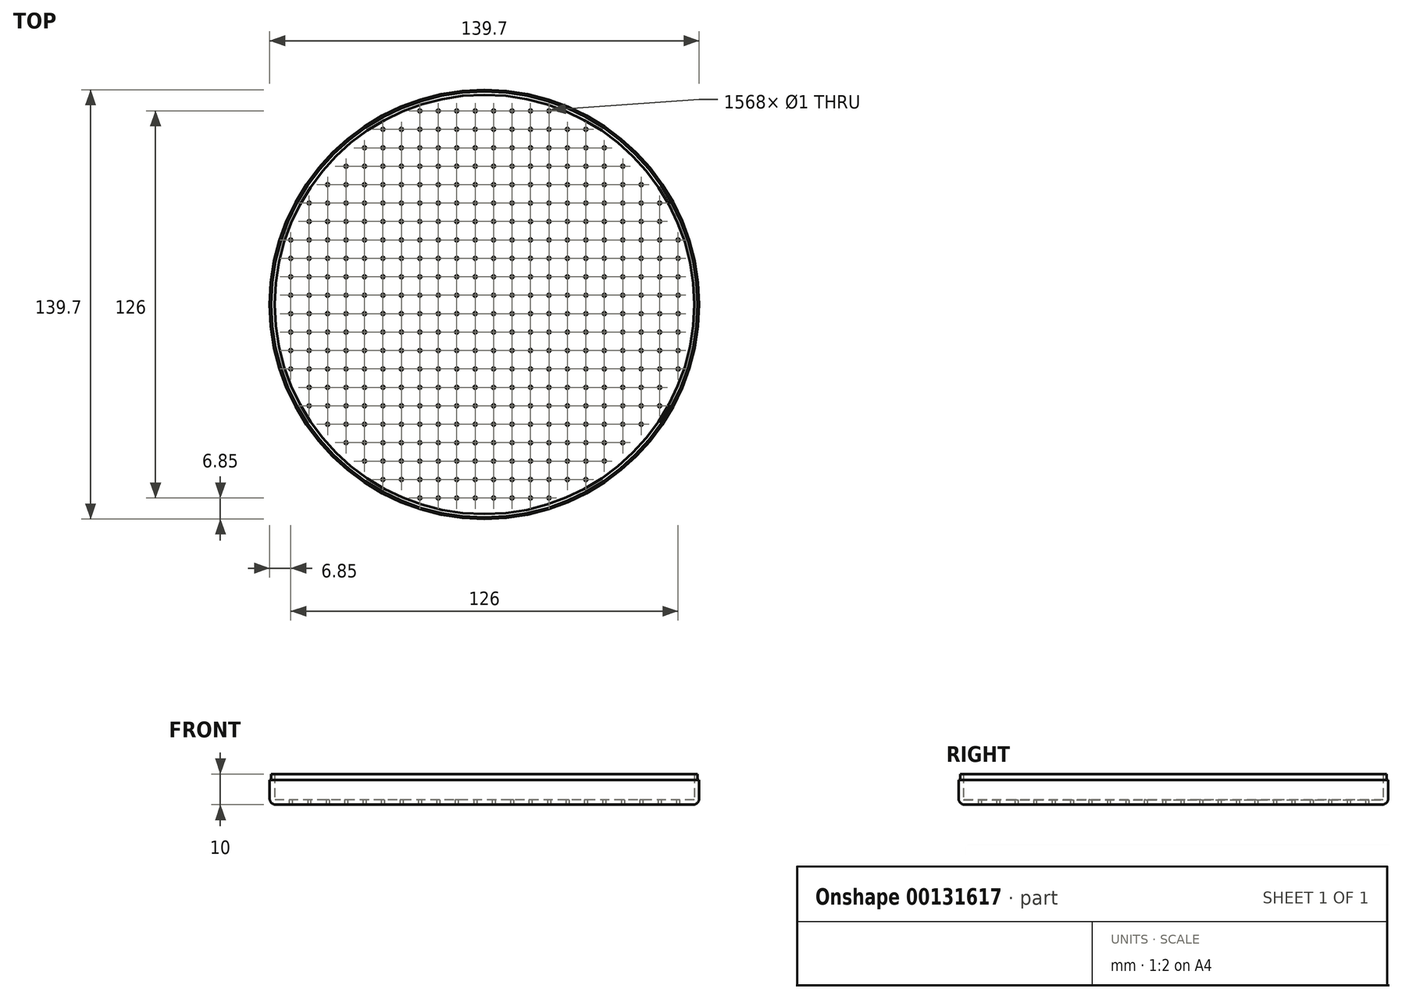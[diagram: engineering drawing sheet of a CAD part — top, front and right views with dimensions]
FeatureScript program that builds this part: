
annotation { "Feature Type Name" : "Feature", "Feature Type Description" : "" }
export const myFeature = defineFeature(function(context is Context, id is Id, definition is map)
    precondition{}
    {
        {
            var Q0;
            Q0=qCreatedBy(makeId("Top.planeOp"),FACE);
            var sketch = newSketch(context, id + "F0", { "sketchPlane" : qUnion([Q0])});
            skCircle(sketch, "E0", {"center": v(0, 0) * mm, "radius": 69.85 * mm});
            skSolve(sketch);
        }
        {
            var Q0;
            Q0 = qSketchRegion(id + "F0", true);
            extrude(context, id + "F1", {"entities" : qUnion([Q0]), "depth" : 10 * mm});
        }
        {
            var Q0;
            Q0=makeQuery(id+"F1.opExtrude","CAP_FACE",FACE,{"disambiguationData":[OSD([sQuery(id+"F0.wireOp",EDGE,"E0")])],"isStart":false});
            shell(context, id + "F2", {"entities" : qUnion([Q0]), "thickness" : 1.6 * mm});
        }
        {
            var Q0;
            Q0=makeQuery(id+"F1.opExtrude","CAP_FACE",FACE,{"disambiguationData":[OSD([sQuery(id+"F0.wireOp",EDGE,"E0")])],"isStart":true});
            var sketch = newSketch(context, id + "F3", { "sketchPlane" : qUnion([Q0])});
            skCircle(sketch, "E1", {"center": v(-3, 3) * mm, "radius": 0.5 * mm});
            skCircle(sketch, "E2.0.1.0", {"center": v(-3, 9) * mm, "radius": 0.5 * mm});
            skCircle(sketch, "E2.0.2.0", {"center": v(-3, 15) * mm, "radius": 0.5 * mm});
            skCircle(sketch, "E2.0.3.0", {"center": v(-3, 21) * mm, "radius": 0.5 * mm});
            skCircle(sketch, "E2.0.4.0", {"center": v(-3, 27) * mm, "radius": 0.5 * mm});
            skCircle(sketch, "E2.0.5.0", {"center": v(-3, 33) * mm, "radius": 0.5 * mm});
            skCircle(sketch, "E2.0.6.0", {"center": v(-3, 39) * mm, "radius": 0.5 * mm});
            skCircle(sketch, "E2.0.7.0", {"center": v(-3, 45) * mm, "radius": 0.5 * mm});
            skCircle(sketch, "E2.0.8.0", {"center": v(-3, 51) * mm, "radius": 0.5 * mm});
            skCircle(sketch, "E2.0.9.0", {"center": v(-3, 57) * mm, "radius": 0.5 * mm});
            skCircle(sketch, "E2.0.10.0", {"center": v(-3, 63) * mm, "radius": 0.5 * mm});
            skCircle(sketch, "E2.1.0.0", {"center": v(-9, 3) * mm, "radius": 0.5 * mm});
            skCircle(sketch, "E2.1.1.0", {"center": v(-9, 9) * mm, "radius": 0.5 * mm});
            skCircle(sketch, "E2.1.2.0", {"center": v(-9, 15) * mm, "radius": 0.5 * mm});
            skCircle(sketch, "E2.1.3.0", {"center": v(-9, 21) * mm, "radius": 0.5 * mm});
            skCircle(sketch, "E2.1.4.0", {"center": v(-9, 27) * mm, "radius": 0.5 * mm});
            skCircle(sketch, "E2.1.5.0", {"center": v(-9, 33) * mm, "radius": 0.5 * mm});
            skCircle(sketch, "E2.1.6.0", {"center": v(-9, 39) * mm, "radius": 0.5 * mm});
            skCircle(sketch, "E2.1.7.0", {"center": v(-9, 45) * mm, "radius": 0.5 * mm});
            skCircle(sketch, "E2.1.8.0", {"center": v(-9, 51) * mm, "radius": 0.5 * mm});
            skCircle(sketch, "E2.1.9.0", {"center": v(-9, 57) * mm, "radius": 0.5 * mm});
            skCircle(sketch, "E2.1.10.0", {"center": v(-9, 63) * mm, "radius": 0.5 * mm});
            skCircle(sketch, "E2.2.0.0", {"center": v(-15, 3) * mm, "radius": 0.5 * mm});
            skCircle(sketch, "E2.2.1.0", {"center": v(-15, 9) * mm, "radius": 0.5 * mm});
            skCircle(sketch, "E2.2.2.0", {"center": v(-15, 15) * mm, "radius": 0.5 * mm});
            skCircle(sketch, "E2.2.3.0", {"center": v(-15, 21) * mm, "radius": 0.5 * mm});
            skCircle(sketch, "E2.2.4.0", {"center": v(-15, 27) * mm, "radius": 0.5 * mm});
            skCircle(sketch, "E2.2.5.0", {"center": v(-15, 33) * mm, "radius": 0.5 * mm});
            skCircle(sketch, "E2.2.6.0", {"center": v(-15, 39) * mm, "radius": 0.5 * mm});
            skCircle(sketch, "E2.2.7.0", {"center": v(-15, 45) * mm, "radius": 0.5 * mm});
            skCircle(sketch, "E2.2.8.0", {"center": v(-15, 51) * mm, "radius": 0.5 * mm});
            skCircle(sketch, "E2.2.9.0", {"center": v(-15, 57) * mm, "radius": 0.5 * mm});
            skCircle(sketch, "E2.2.10.0", {"center": v(-15, 63) * mm, "radius": 0.5 * mm});
            skCircle(sketch, "E2.3.0.0", {"center": v(-21, 3) * mm, "radius": 0.5 * mm});
            skCircle(sketch, "E2.3.1.0", {"center": v(-21, 9) * mm, "radius": 0.5 * mm});
            skCircle(sketch, "E2.3.2.0", {"center": v(-21, 15) * mm, "radius": 0.5 * mm});
            skCircle(sketch, "E2.3.3.0", {"center": v(-21, 21) * mm, "radius": 0.5 * mm});
            skCircle(sketch, "E2.3.4.0", {"center": v(-21, 27) * mm, "radius": 0.5 * mm});
            skCircle(sketch, "E2.3.5.0", {"center": v(-21, 33) * mm, "radius": 0.5 * mm});
            skCircle(sketch, "E2.3.6.0", {"center": v(-21, 39) * mm, "radius": 0.5 * mm});
            skCircle(sketch, "E2.3.7.0", {"center": v(-21, 45) * mm, "radius": 0.5 * mm});
            skCircle(sketch, "E2.3.8.0", {"center": v(-21, 51) * mm, "radius": 0.5 * mm});
            skCircle(sketch, "E2.3.9.0", {"center": v(-21, 57) * mm, "radius": 0.5 * mm});
            skCircle(sketch, "E2.3.10.0", {"center": v(-21, 63) * mm, "radius": 0.5 * mm});
            skCircle(sketch, "E2.4.0.0", {"center": v(-27, 3) * mm, "radius": 0.5 * mm});
            skCircle(sketch, "E2.4.1.0", {"center": v(-27, 9) * mm, "radius": 0.5 * mm});
            skCircle(sketch, "E2.4.2.0", {"center": v(-27, 15) * mm, "radius": 0.5 * mm});
            skCircle(sketch, "E2.4.3.0", {"center": v(-27, 21) * mm, "radius": 0.5 * mm});
            skCircle(sketch, "E2.4.4.0", {"center": v(-27, 27) * mm, "radius": 0.5 * mm});
            skCircle(sketch, "E2.4.5.0", {"center": v(-27, 33) * mm, "radius": 0.5 * mm});
            skCircle(sketch, "E2.4.6.0", {"center": v(-27, 39) * mm, "radius": 0.5 * mm});
            skCircle(sketch, "E2.4.7.0", {"center": v(-27, 45) * mm, "radius": 0.5 * mm});
            skCircle(sketch, "E2.4.8.0", {"center": v(-27, 51) * mm, "radius": 0.5 * mm});
            skCircle(sketch, "E2.4.9.0", {"center": v(-27, 57) * mm, "radius": 0.5 * mm});
            skCircle(sketch, "E2.5.0.0", {"center": v(-33, 3) * mm, "radius": 0.5 * mm});
            skCircle(sketch, "E2.5.1.0", {"center": v(-33, 9) * mm, "radius": 0.5 * mm});
            skCircle(sketch, "E2.5.2.0", {"center": v(-33, 15) * mm, "radius": 0.5 * mm});
            skCircle(sketch, "E2.5.3.0", {"center": v(-33, 21) * mm, "radius": 0.5 * mm});
            skCircle(sketch, "E2.5.4.0", {"center": v(-33, 27) * mm, "radius": 0.5 * mm});
            skCircle(sketch, "E2.5.5.0", {"center": v(-33, 33) * mm, "radius": 0.5 * mm});
            skCircle(sketch, "E2.5.6.0", {"center": v(-33, 39) * mm, "radius": 0.5 * mm});
            skCircle(sketch, "E2.5.7.0", {"center": v(-33, 45) * mm, "radius": 0.5 * mm});
            skCircle(sketch, "E2.5.8.0", {"center": v(-33, 51) * mm, "radius": 0.5 * mm});
            skCircle(sketch, "E2.5.9.0", {"center": v(-33, 57) * mm, "radius": 0.5 * mm});
            skCircle(sketch, "E2.6.0.0", {"center": v(-39, 3) * mm, "radius": 0.5 * mm});
            skCircle(sketch, "E2.6.1.0", {"center": v(-39, 9) * mm, "radius": 0.5 * mm});
            skCircle(sketch, "E2.6.2.0", {"center": v(-39, 15) * mm, "radius": 0.5 * mm});
            skCircle(sketch, "E2.6.3.0", {"center": v(-39, 21) * mm, "radius": 0.5 * mm});
            skCircle(sketch, "E2.6.4.0", {"center": v(-39, 27) * mm, "radius": 0.5 * mm});
            skCircle(sketch, "E2.6.5.0", {"center": v(-39, 33) * mm, "radius": 0.5 * mm});
            skCircle(sketch, "E2.6.6.0", {"center": v(-39, 39) * mm, "radius": 0.5 * mm});
            skCircle(sketch, "E2.6.7.0", {"center": v(-39, 45) * mm, "radius": 0.5 * mm});
            skCircle(sketch, "E2.6.8.0", {"center": v(-39, 51) * mm, "radius": 0.5 * mm});
            skCircle(sketch, "E2.7.0.0", {"center": v(-45, 3) * mm, "radius": 0.5 * mm});
            skCircle(sketch, "E2.7.1.0", {"center": v(-45, 9) * mm, "radius": 0.5 * mm});
            skCircle(sketch, "E2.7.2.0", {"center": v(-45, 15) * mm, "radius": 0.5 * mm});
            skCircle(sketch, "E2.7.3.0", {"center": v(-45, 21) * mm, "radius": 0.5 * mm});
            skCircle(sketch, "E2.7.4.0", {"center": v(-45, 27) * mm, "radius": 0.5 * mm});
            skCircle(sketch, "E2.7.5.0", {"center": v(-45, 33) * mm, "radius": 0.5 * mm});
            skCircle(sketch, "E2.7.6.0", {"center": v(-45, 39) * mm, "radius": 0.5 * mm});
            skCircle(sketch, "E2.7.7.0", {"center": v(-45, 45) * mm, "radius": 0.5 * mm});
            skCircle(sketch, "E2.8.0.0", {"center": v(-51, 3) * mm, "radius": 0.5 * mm});
            skCircle(sketch, "E2.8.1.0", {"center": v(-51, 9) * mm, "radius": 0.5 * mm});
            skCircle(sketch, "E2.8.2.0", {"center": v(-51, 15) * mm, "radius": 0.5 * mm});
            skCircle(sketch, "E2.8.3.0", {"center": v(-51, 21) * mm, "radius": 0.5 * mm});
            skCircle(sketch, "E2.8.4.0", {"center": v(-51, 27) * mm, "radius": 0.5 * mm});
            skCircle(sketch, "E2.8.5.0", {"center": v(-51, 33) * mm, "radius": 0.5 * mm});
            skCircle(sketch, "E2.8.6.0", {"center": v(-51, 39) * mm, "radius": 0.5 * mm});
            skCircle(sketch, "E2.9.0.0", {"center": v(-57, 3) * mm, "radius": 0.5 * mm});
            skCircle(sketch, "E2.9.1.0", {"center": v(-57, 9) * mm, "radius": 0.5 * mm});
            skCircle(sketch, "E2.9.2.0", {"center": v(-57, 15) * mm, "radius": 0.5 * mm});
            skCircle(sketch, "E2.9.3.0", {"center": v(-57, 21) * mm, "radius": 0.5 * mm});
            skCircle(sketch, "E2.9.4.0", {"center": v(-57, 27) * mm, "radius": 0.5 * mm});
            skCircle(sketch, "E2.9.5.0", {"center": v(-57, 33) * mm, "radius": 0.5 * mm});
            skCircle(sketch, "E2.10.0.0", {"center": v(-63, 3) * mm, "radius": 0.5 * mm});
            skCircle(sketch, "E2.10.1.0", {"center": v(-63, 9) * mm, "radius": 0.5 * mm});
            skCircle(sketch, "E2.10.2.0", {"center": v(-63, 15) * mm, "radius": 0.5 * mm});
            skCircle(sketch, "E2.10.3.0", {"center": v(-63, 21) * mm, "radius": 0.5 * mm});
            skLineSegment(sketch, "E2.direction1", {"start": v(-3, 3) * mm, "end": v(-9, 3) * mm, "construction": true});
            skLineSegment(sketch, "E2.direction2", {"start": v(-3, 3) * mm, "end": v(-3, 9) * mm, "construction": true});
            skCircle(sketch, "E3.MirrorC", {"center": v(-3, -3) * mm, "radius": 0.5 * mm});
            skCircle(sketch, "E4.MirrorC", {"center": v(-9, -3) * mm, "radius": 0.5 * mm});
            skCircle(sketch, "E5.MirrorC", {"center": v(-3, -9) * mm, "radius": 0.5 * mm});
            skCircle(sketch, "E6.MirrorC", {"center": v(-51, -27) * mm, "radius": 0.5 * mm});
            skCircle(sketch, "E7.MirrorC", {"center": v(-57, -9) * mm, "radius": 0.5 * mm});
            skCircle(sketch, "E8.MirrorC", {"center": v(-21, -3) * mm, "radius": 0.5 * mm});
            skCircle(sketch, "E9.MirrorC", {"center": v(-15, -33) * mm, "radius": 0.5 * mm});
            skCircle(sketch, "E10.MirrorC", {"center": v(-27, -27) * mm, "radius": 0.5 * mm});
            skCircle(sketch, "E11.MirrorC", {"center": v(-21, -57) * mm, "radius": 0.5 * mm});
            skCircle(sketch, "E12.MirrorC", {"center": v(-33, -51) * mm, "radius": 0.5 * mm});
            skCircle(sketch, "E13.MirrorC", {"center": v(-33, -9) * mm, "radius": 0.5 * mm});
            skCircle(sketch, "E14.MirrorC", {"center": v(-45, -3) * mm, "radius": 0.5 * mm});
            skCircle(sketch, "E15.MirrorC", {"center": v(-39, -33) * mm, "radius": 0.5 * mm});
            skCircle(sketch, "E16.MirrorC", {"center": v(-9, -51) * mm, "radius": 0.5 * mm});
            skCircle(sketch, "E17.MirrorC", {"center": v(-39, -21) * mm, "radius": 0.5 * mm});
            skCircle(sketch, "E18.MirrorC", {"center": v(-45, -45) * mm, "radius": 0.5 * mm});
            skCircle(sketch, "E19.MirrorC", {"center": v(-63, -21) * mm, "radius": 0.5 * mm});
            skCircle(sketch, "E20.MirrorC", {"center": v(-15, -21) * mm, "radius": 0.5 * mm});
            skCircle(sketch, "E21.MirrorC", {"center": v(-21, -45) * mm, "radius": 0.5 * mm});
            skCircle(sketch, "E22.MirrorC", {"center": v(-51, -21) * mm, "radius": 0.5 * mm});
            skCircle(sketch, "E23.MirrorC", {"center": v(-27, -21) * mm, "radius": 0.5 * mm});
            skCircle(sketch, "E24.MirrorC", {"center": v(-33, -45) * mm, "radius": 0.5 * mm});
            skCircle(sketch, "E25.MirrorC", {"center": v(-9, -45) * mm, "radius": 0.5 * mm});
            skCircle(sketch, "E26.MirrorC", {"center": v(-39, -15) * mm, "radius": 0.5 * mm});
            skCircle(sketch, "E27.MirrorC", {"center": v(-45, -39) * mm, "radius": 0.5 * mm});
            skCircle(sketch, "E28.MirrorC", {"center": v(-63, -15) * mm, "radius": 0.5 * mm});
            skCircle(sketch, "E29.MirrorC", {"center": v(-15, -15) * mm, "radius": 0.5 * mm});
            skCircle(sketch, "E30.MirrorC", {"center": v(-21, -39) * mm, "radius": 0.5 * mm});
            skCircle(sketch, "E31.MirrorC", {"center": v(-3, -63) * mm, "radius": 0.5 * mm});
            skCircle(sketch, "E32.MirrorC", {"center": v(-3, -57) * mm, "radius": 0.5 * mm});
            skCircle(sketch, "E33.MirrorC", {"center": v(-3, -51) * mm, "radius": 0.5 * mm});
            skCircle(sketch, "E34.MirrorC", {"center": v(-3, -45) * mm, "radius": 0.5 * mm});
            skCircle(sketch, "E35.MirrorC", {"center": v(-3, -39) * mm, "radius": 0.5 * mm});
            skCircle(sketch, "E36.MirrorC", {"center": v(-3, -33) * mm, "radius": 0.5 * mm});
            skCircle(sketch, "E37.MirrorC", {"center": v(-3, -27) * mm, "radius": 0.5 * mm});
            skCircle(sketch, "E38.MirrorC", {"center": v(-3, -21) * mm, "radius": 0.5 * mm});
            skCircle(sketch, "E39.MirrorC", {"center": v(-3, -15) * mm, "radius": 0.5 * mm});
            skCircle(sketch, "E40.MirrorC", {"center": v(-51, -15) * mm, "radius": 0.5 * mm});
            skCircle(sketch, "E41.MirrorC", {"center": v(-15, -63) * mm, "radius": 0.5 * mm});
            skCircle(sketch, "E42.MirrorC", {"center": v(-27, -15) * mm, "radius": 0.5 * mm});
            skCircle(sketch, "E43.MirrorC", {"center": v(-33, -39) * mm, "radius": 0.5 * mm});
            skCircle(sketch, "E44.MirrorC", {"center": v(-9, -21) * mm, "radius": 0.5 * mm});
            skCircle(sketch, "E45.MirrorC", {"center": v(-9, -15) * mm, "radius": 0.5 * mm});
            skCircle(sketch, "E46.MirrorC", {"center": v(-9, -39) * mm, "radius": 0.5 * mm});
            skCircle(sketch, "E47.MirrorC", {"center": v(-9, -9) * mm, "radius": 0.5 * mm});
            skCircle(sketch, "E48.MirrorC", {"center": v(-39, -9) * mm, "radius": 0.5 * mm});
            skCircle(sketch, "E49.MirrorC", {"center": v(-45, -33) * mm, "radius": 0.5 * mm});
            skCircle(sketch, "E50.MirrorC", {"center": v(-63, -9) * mm, "radius": 0.5 * mm});
            skCircle(sketch, "E51.MirrorC", {"center": v(-15, -9) * mm, "radius": 0.5 * mm});
            skCircle(sketch, "E52.MirrorC", {"center": v(-21, -33) * mm, "radius": 0.5 * mm});
            skCircle(sketch, "E53.MirrorC", {"center": v(-27, -57) * mm, "radius": 0.5 * mm});
            skCircle(sketch, "E54.MirrorC", {"center": v(-15, -57) * mm, "radius": 0.5 * mm});
            skCircle(sketch, "E55.MirrorC", {"center": v(-27, -9) * mm, "radius": 0.5 * mm});
            skCircle(sketch, "E56.MirrorC", {"center": v(-33, -33) * mm, "radius": 0.5 * mm});
            skCircle(sketch, "E57.MirrorC", {"center": v(-9, -33) * mm, "radius": 0.5 * mm});
            skCircle(sketch, "E58.MirrorC", {"center": v(-39, -3) * mm, "radius": 0.5 * mm});
            skCircle(sketch, "E59.MirrorC", {"center": v(-45, -27) * mm, "radius": 0.5 * mm});
            skCircle(sketch, "E60.MirrorC", {"center": v(-63, -3) * mm, "radius": 0.5 * mm});
            skCircle(sketch, "E61.MirrorC", {"center": v(-15, -3) * mm, "radius": 0.5 * mm});
            skCircle(sketch, "E62.MirrorC", {"center": v(-21, -27) * mm, "radius": 0.5 * mm});
            skCircle(sketch, "E63.MirrorC", {"center": v(-27, -51) * mm, "radius": 0.5 * mm});
            skCircle(sketch, "E64.MirrorC", {"center": v(-51, -9) * mm, "radius": 0.5 * mm});
            skCircle(sketch, "E65.MirrorC", {"center": v(-57, -33) * mm, "radius": 0.5 * mm});
            skCircle(sketch, "E66.MirrorC", {"center": v(-45, -21) * mm, "radius": 0.5 * mm});
            skCircle(sketch, "E67.MirrorC", {"center": v(-9, -27) * mm, "radius": 0.5 * mm});
            skCircle(sketch, "E68.MirrorC", {"center": v(-21, -21) * mm, "radius": 0.5 * mm});
            skCircle(sketch, "E69.MirrorC", {"center": v(-27, -45) * mm, "radius": 0.5 * mm});
            skCircle(sketch, "E70.MirrorC", {"center": v(-51, -3) * mm, "radius": 0.5 * mm});
            skCircle(sketch, "E71.MirrorC", {"center": v(-57, -27) * mm, "radius": 0.5 * mm});
            skLineSegment(sketch, "E72.MirrorCS", {"start": v(-3, -3) * mm, "end": v(-3, -9) * mm, "construction": true});
            skLineSegment(sketch, "E73.MirrorCS", {"start": v(-3, -3) * mm, "end": v(-9, -3) * mm, "construction": true});
            skCircle(sketch, "E74.MirrorC", {"center": v(-15, -51) * mm, "radius": 0.5 * mm});
            skCircle(sketch, "E75.MirrorC", {"center": v(-27, -3) * mm, "radius": 0.5 * mm});
            skCircle(sketch, "E76.MirrorC", {"center": v(-33, -27) * mm, "radius": 0.5 * mm});
            skCircle(sketch, "E77.MirrorC", {"center": v(-39, -51) * mm, "radius": 0.5 * mm});
            skCircle(sketch, "E78.MirrorC", {"center": v(-51, -39) * mm, "radius": 0.5 * mm});
            skCircle(sketch, "E79.MirrorC", {"center": v(-57, -21) * mm, "radius": 0.5 * mm});
            skCircle(sketch, "E80.MirrorC", {"center": v(-21, -15) * mm, "radius": 0.5 * mm});
            skCircle(sketch, "E81.MirrorC", {"center": v(-15, -45) * mm, "radius": 0.5 * mm});
            skCircle(sketch, "E82.MirrorC", {"center": v(-27, -39) * mm, "radius": 0.5 * mm});
            skCircle(sketch, "E83.MirrorC", {"center": v(-33, -21) * mm, "radius": 0.5 * mm});
            skCircle(sketch, "E84.MirrorC", {"center": v(-45, -15) * mm, "radius": 0.5 * mm});
            skCircle(sketch, "E85.MirrorC", {"center": v(-39, -45) * mm, "radius": 0.5 * mm});
            skCircle(sketch, "E86.MirrorC", {"center": v(-9, -63) * mm, "radius": 0.5 * mm});
            skCircle(sketch, "E87.MirrorC", {"center": v(-51, -33) * mm, "radius": 0.5 * mm});
            skCircle(sketch, "E88.MirrorC", {"center": v(-57, -15) * mm, "radius": 0.5 * mm});
            skCircle(sketch, "E89.MirrorC", {"center": v(-21, -9) * mm, "radius": 0.5 * mm});
            skCircle(sketch, "E90.MirrorC", {"center": v(-15, -39) * mm, "radius": 0.5 * mm});
            skCircle(sketch, "E91.MirrorC", {"center": v(-27, -33) * mm, "radius": 0.5 * mm});
            skCircle(sketch, "E92.MirrorC", {"center": v(-21, -63) * mm, "radius": 0.5 * mm});
            skCircle(sketch, "E93.MirrorC", {"center": v(-33, -57) * mm, "radius": 0.5 * mm});
            skCircle(sketch, "E94.MirrorC", {"center": v(-33, -15) * mm, "radius": 0.5 * mm});
            skCircle(sketch, "E95.MirrorC", {"center": v(-45, -9) * mm, "radius": 0.5 * mm});
            skCircle(sketch, "E96.MirrorC", {"center": v(-39, -39) * mm, "radius": 0.5 * mm});
            skCircle(sketch, "E97.MirrorC", {"center": v(-9, -57) * mm, "radius": 0.5 * mm});
            skCircle(sketch, "E98.MirrorC", {"center": v(-39, -27) * mm, "radius": 0.5 * mm});
            skCircle(sketch, "E99.MirrorC", {"center": v(-57, -3) * mm, "radius": 0.5 * mm});
            skCircle(sketch, "E100.MirrorC", {"center": v(-15, -27) * mm, "radius": 0.5 * mm});
            skCircle(sketch, "E101.MirrorC", {"center": v(-21, -51) * mm, "radius": 0.5 * mm});
            skCircle(sketch, "E102.MirrorC", {"center": v(-33, -3) * mm, "radius": 0.5 * mm});
            skCircle(sketch, "E103.MirrorC", {"center": v(3, 3) * mm, "radius": 0.5 * mm});
            skCircle(sketch, "E104.MirrorC", {"center": v(3, -3) * mm, "radius": 0.5 * mm});
            skCircle(sketch, "E105.MirrorC", {"center": v(9, 3) * mm, "radius": 0.5 * mm});
            skCircle(sketch, "E106.MirrorC", {"center": v(3, 9) * mm, "radius": 0.5 * mm});
            skLineSegment(sketch, "E107.MirrorCS", {"start": v(3, -3) * mm, "end": v(9, -3) * mm, "construction": true});
            skLineSegment(sketch, "E108.MirrorCS", {"start": v(3, -3) * mm, "end": v(3, -9) * mm, "construction": true});
            skLineSegment(sketch, "E109.MirrorCS", {"start": v(3, 3) * mm, "end": v(3, 9) * mm, "construction": true});
            skLineSegment(sketch, "E110.MirrorCS", {"start": v(3, 3) * mm, "end": v(9, 3) * mm, "construction": true});
            skCircle(sketch, "E111.MirrorC", {"center": v(3, -9) * mm, "radius": 0.5 * mm});
            skCircle(sketch, "E112.MirrorC", {"center": v(9, -3) * mm, "radius": 0.5 * mm});
            skCircle(sketch, "E113.MirrorC", {"center": v(3, 63) * mm, "radius": 0.5 * mm});
            skCircle(sketch, "E114.MirrorC", {"center": v(3, 57) * mm, "radius": 0.5 * mm});
            skCircle(sketch, "E115.MirrorC", {"center": v(3, 51) * mm, "radius": 0.5 * mm});
            skCircle(sketch, "E116.MirrorC", {"center": v(3, 45) * mm, "radius": 0.5 * mm});
            skCircle(sketch, "E117.MirrorC", {"center": v(3, 39) * mm, "radius": 0.5 * mm});
            skCircle(sketch, "E118.MirrorC", {"center": v(3, 33) * mm, "radius": 0.5 * mm});
            skCircle(sketch, "E119.MirrorC", {"center": v(3, 27) * mm, "radius": 0.5 * mm});
            skCircle(sketch, "E120.MirrorC", {"center": v(3, 21) * mm, "radius": 0.5 * mm});
            skCircle(sketch, "E121.MirrorC", {"center": v(3, 15) * mm, "radius": 0.5 * mm});
            skCircle(sketch, "E122.MirrorC", {"center": v(9, 21) * mm, "radius": 0.5 * mm});
            skCircle(sketch, "E123.MirrorC", {"center": v(9, 15) * mm, "radius": 0.5 * mm});
            skCircle(sketch, "E124.MirrorC", {"center": v(9, 9) * mm, "radius": 0.5 * mm});
            skCircle(sketch, "E125.MirrorC", {"center": v(51, -33) * mm, "radius": 0.5 * mm});
            skCircle(sketch, "E126.MirrorC", {"center": v(33, -39) * mm, "radius": 0.5 * mm});
            skCircle(sketch, "E127.MirrorC", {"center": v(27, -9) * mm, "radius": 0.5 * mm});
            skCircle(sketch, "E128.MirrorC", {"center": v(45, -21) * mm, "radius": 0.5 * mm});
            skCircle(sketch, "E129.MirrorC", {"center": v(51, -39) * mm, "radius": 0.5 * mm});
            skCircle(sketch, "E130.MirrorC", {"center": v(21, -3) * mm, "radius": 0.5 * mm});
            skCircle(sketch, "E131.MirrorC", {"center": v(39, 27) * mm, "radius": 0.5 * mm});
            skCircle(sketch, "E132.MirrorC", {"center": v(57, 3) * mm, "radius": 0.5 * mm});
            skCircle(sketch, "E133.MirrorC", {"center": v(15, 27) * mm, "radius": 0.5 * mm});
            skCircle(sketch, "E134.MirrorC", {"center": v(21, 51) * mm, "radius": 0.5 * mm});
            skCircle(sketch, "E135.MirrorC", {"center": v(33, 3) * mm, "radius": 0.5 * mm});
            skCircle(sketch, "E136.MirrorC", {"center": v(9, -63) * mm, "radius": 0.5 * mm});
            skCircle(sketch, "E137.MirrorC", {"center": v(9, -57) * mm, "radius": 0.5 * mm});
            skCircle(sketch, "E138.MirrorC", {"center": v(27, -15) * mm, "radius": 0.5 * mm});
            skCircle(sketch, "E139.MirrorC", {"center": v(15, -57) * mm, "radius": 0.5 * mm});
            skCircle(sketch, "E140.MirrorC", {"center": v(39, -51) * mm, "radius": 0.5 * mm});
            skCircle(sketch, "E141.MirrorC", {"center": v(21, -45) * mm, "radius": 0.5 * mm});
            skCircle(sketch, "E142.MirrorC", {"center": v(21, -39) * mm, "radius": 0.5 * mm});
            skCircle(sketch, "E143.MirrorC", {"center": v(39, 21) * mm, "radius": 0.5 * mm});
            skCircle(sketch, "E144.MirrorC", {"center": v(45, 45) * mm, "radius": 0.5 * mm});
            skCircle(sketch, "E145.MirrorC", {"center": v(63, 21) * mm, "radius": 0.5 * mm});
            skCircle(sketch, "E146.MirrorC", {"center": v(15, 21) * mm, "radius": 0.5 * mm});
            skCircle(sketch, "E147.MirrorC", {"center": v(21, 45) * mm, "radius": 0.5 * mm});
            skCircle(sketch, "E148.MirrorC", {"center": v(39, -45) * mm, "radius": 0.5 * mm});
            skCircle(sketch, "E149.MirrorC", {"center": v(39, -39) * mm, "radius": 0.5 * mm});
            skCircle(sketch, "E150.MirrorC", {"center": v(15, -63) * mm, "radius": 0.5 * mm});
            skCircle(sketch, "E151.MirrorC", {"center": v(33, -27) * mm, "radius": 0.5 * mm});
            skCircle(sketch, "E152.MirrorC", {"center": v(15, -21) * mm, "radius": 0.5 * mm});
            skCircle(sketch, "E153.MirrorC", {"center": v(15, -15) * mm, "radius": 0.5 * mm});
            skCircle(sketch, "E154.MirrorC", {"center": v(39, 15) * mm, "radius": 0.5 * mm});
            skCircle(sketch, "E155.MirrorC", {"center": v(45, 39) * mm, "radius": 0.5 * mm});
            skCircle(sketch, "E156.MirrorC", {"center": v(63, 15) * mm, "radius": 0.5 * mm});
            skCircle(sketch, "E157.MirrorC", {"center": v(15, 15) * mm, "radius": 0.5 * mm});
            skCircle(sketch, "E158.MirrorC", {"center": v(21, 39) * mm, "radius": 0.5 * mm});
            skCircle(sketch, "E159.MirrorC", {"center": v(45, -15) * mm, "radius": 0.5 * mm});
            skCircle(sketch, "E160.MirrorC", {"center": v(45, -9) * mm, "radius": 0.5 * mm});
            skCircle(sketch, "E161.MirrorC", {"center": v(27, -57) * mm, "radius": 0.5 * mm});
            skCircle(sketch, "E162.MirrorC", {"center": v(27, -3) * mm, "radius": 0.5 * mm});
            skCircle(sketch, "E163.MirrorC", {"center": v(63, -21) * mm, "radius": 0.5 * mm});
            skCircle(sketch, "E164.MirrorC", {"center": v(63, -15) * mm, "radius": 0.5 * mm});
            skCircle(sketch, "E165.MirrorC", {"center": v(39, 9) * mm, "radius": 0.5 * mm});
            skCircle(sketch, "E166.MirrorC", {"center": v(45, 33) * mm, "radius": 0.5 * mm});
            skCircle(sketch, "E167.MirrorC", {"center": v(63, 9) * mm, "radius": 0.5 * mm});
            skCircle(sketch, "E168.MirrorC", {"center": v(15, 9) * mm, "radius": 0.5 * mm});
            skCircle(sketch, "E169.MirrorC", {"center": v(21, 33) * mm, "radius": 0.5 * mm});
            skCircle(sketch, "E170.MirrorC", {"center": v(27, 57) * mm, "radius": 0.5 * mm});
            skCircle(sketch, "E171.MirrorC", {"center": v(33, -21) * mm, "radius": 0.5 * mm});
            skCircle(sketch, "E172.MirrorC", {"center": v(33, -15) * mm, "radius": 0.5 * mm});
            skCircle(sketch, "E173.MirrorC", {"center": v(21, -33) * mm, "radius": 0.5 * mm});
            skCircle(sketch, "E174.MirrorC", {"center": v(57, -33) * mm, "radius": 0.5 * mm});
            skCircle(sketch, "E175.MirrorC", {"center": v(15, -51) * mm, "radius": 0.5 * mm});
            skCircle(sketch, "E176.MirrorC", {"center": v(57, -9) * mm, "radius": 0.5 * mm});
            skCircle(sketch, "E177.MirrorC", {"center": v(39, 3) * mm, "radius": 0.5 * mm});
            skCircle(sketch, "E178.MirrorC", {"center": v(45, 27) * mm, "radius": 0.5 * mm});
            skCircle(sketch, "E179.MirrorC", {"center": v(63, 3) * mm, "radius": 0.5 * mm});
            skCircle(sketch, "E180.MirrorC", {"center": v(15, 3) * mm, "radius": 0.5 * mm});
            skCircle(sketch, "E181.MirrorC", {"center": v(21, 27) * mm, "radius": 0.5 * mm});
            skCircle(sketch, "E182.MirrorC", {"center": v(27, 51) * mm, "radius": 0.5 * mm});
            skCircle(sketch, "E183.MirrorC", {"center": v(33, -57) * mm, "radius": 0.5 * mm});
            skCircle(sketch, "E184.MirrorC", {"center": v(51, -15) * mm, "radius": 0.5 * mm});
            skCircle(sketch, "E185.MirrorC", {"center": v(15, -9) * mm, "radius": 0.5 * mm});
            skCircle(sketch, "E186.MirrorC", {"center": v(51, -9) * mm, "radius": 0.5 * mm});
            skCircle(sketch, "E187.MirrorC", {"center": v(45, -45) * mm, "radius": 0.5 * mm});
            skCircle(sketch, "E188.MirrorC", {"center": v(45, -39) * mm, "radius": 0.5 * mm});
            skCircle(sketch, "E189.MirrorC", {"center": v(45, 21) * mm, "radius": 0.5 * mm});
            skCircle(sketch, "E190.MirrorC", {"center": v(39, 51) * mm, "radius": 0.5 * mm});
            skCircle(sketch, "E191.MirrorC", {"center": v(33, 27) * mm, "radius": 0.5 * mm});
            skCircle(sketch, "E192.MirrorC", {"center": v(27, -51) * mm, "radius": 0.5 * mm});
            skCircle(sketch, "E193.MirrorC", {"center": v(27, 3) * mm, "radius": 0.5 * mm});
            skCircle(sketch, "E194.MirrorC", {"center": v(15, 51) * mm, "radius": 0.5 * mm});
            skCircle(sketch, "E195.MirrorC", {"center": v(57, 27) * mm, "radius": 0.5 * mm});
            skCircle(sketch, "E196.MirrorC", {"center": v(51, 3) * mm, "radius": 0.5 * mm});
            skCircle(sketch, "E197.MirrorC", {"center": v(9, -39) * mm, "radius": 0.5 * mm});
            skCircle(sketch, "E198.MirrorC", {"center": v(3, -51) * mm, "radius": 0.5 * mm});
            skCircle(sketch, "E199.MirrorC", {"center": v(33, -51) * mm, "radius": 0.5 * mm});
            skCircle(sketch, "E200.MirrorC", {"center": v(39, -3) * mm, "radius": 0.5 * mm});
            skCircle(sketch, "E201.MirrorC", {"center": v(9, 27) * mm, "radius": 0.5 * mm});
            skCircle(sketch, "E202.MirrorC", {"center": v(39, -27) * mm, "radius": 0.5 * mm});
            skCircle(sketch, "E203.MirrorC", {"center": v(39, 33) * mm, "radius": 0.5 * mm});
            skCircle(sketch, "E204.MirrorC", {"center": v(33, 9) * mm, "radius": 0.5 * mm});
            skCircle(sketch, "E205.MirrorC", {"center": v(21, 57) * mm, "radius": 0.5 * mm});
            skCircle(sketch, "E206.MirrorC", {"center": v(15, 33) * mm, "radius": 0.5 * mm});
            skCircle(sketch, "E207.MirrorC", {"center": v(9, 51) * mm, "radius": 0.5 * mm});
            skCircle(sketch, "E208.MirrorC", {"center": v(57, 9) * mm, "radius": 0.5 * mm});
            skCircle(sketch, "E209.MirrorC", {"center": v(45, 3) * mm, "radius": 0.5 * mm});
            skCircle(sketch, "E210.MirrorC", {"center": v(33, 51) * mm, "radius": 0.5 * mm});
            skCircle(sketch, "E211.MirrorC", {"center": v(57, 33) * mm, "radius": 0.5 * mm});
            skCircle(sketch, "E212.MirrorC", {"center": v(27, 27) * mm, "radius": 0.5 * mm});
            skCircle(sketch, "E213.MirrorC", {"center": v(21, 3) * mm, "radius": 0.5 * mm});
            skCircle(sketch, "E214.MirrorC", {"center": v(9, -21) * mm, "radius": 0.5 * mm});
            skCircle(sketch, "E215.MirrorC", {"center": v(51, 9) * mm, "radius": 0.5 * mm});
            skCircle(sketch, "E216.MirrorC", {"center": v(9, -9) * mm, "radius": 0.5 * mm});
            skCircle(sketch, "E217.MirrorC", {"center": v(3, -45) * mm, "radius": 0.5 * mm});
            skCircle(sketch, "E218.MirrorC", {"center": v(51, -21) * mm, "radius": 0.5 * mm});
            skCircle(sketch, "E219.MirrorC", {"center": v(27, -21) * mm, "radius": 0.5 * mm});
            skCircle(sketch, "E220.MirrorC", {"center": v(51, 27) * mm, "radius": 0.5 * mm});
            skCircle(sketch, "E221.MirrorC", {"center": v(15, -33) * mm, "radius": 0.5 * mm});
            skCircle(sketch, "E222.MirrorC", {"center": v(33, -9) * mm, "radius": 0.5 * mm});
            skCircle(sketch, "E223.MirrorC", {"center": v(33, -33) * mm, "radius": 0.5 * mm});
            skCircle(sketch, "E224.MirrorC", {"center": v(45, -33) * mm, "radius": 0.5 * mm});
            skCircle(sketch, "E225.MirrorC", {"center": v(3, -27) * mm, "radius": 0.5 * mm});
            skCircle(sketch, "E226.MirrorC", {"center": v(9, -51) * mm, "radius": 0.5 * mm});
            skCircle(sketch, "E227.MirrorC", {"center": v(9, -45) * mm, "radius": 0.5 * mm});
            skCircle(sketch, "E228.MirrorC", {"center": v(15, -39) * mm, "radius": 0.5 * mm});
            skCircle(sketch, "E229.MirrorC", {"center": v(15, -45) * mm, "radius": 0.5 * mm});
            skCircle(sketch, "E230.MirrorC", {"center": v(21, -21) * mm, "radius": 0.5 * mm});
            skCircle(sketch, "E231.MirrorC", {"center": v(15, -3) * mm, "radius": 0.5 * mm});
            skCircle(sketch, "E232.MirrorC", {"center": v(57, -27) * mm, "radius": 0.5 * mm});
            skCircle(sketch, "E233.MirrorC", {"center": v(45, -27) * mm, "radius": 0.5 * mm});
            skCircle(sketch, "E234.MirrorC", {"center": v(15, -27) * mm, "radius": 0.5 * mm});
            skCircle(sketch, "E235.MirrorC", {"center": v(39, 39) * mm, "radius": 0.5 * mm});
            skCircle(sketch, "E236.MirrorC", {"center": v(33, 15) * mm, "radius": 0.5 * mm});
            skCircle(sketch, "E237.MirrorC", {"center": v(21, 63) * mm, "radius": 0.5 * mm});
            skCircle(sketch, "E238.MirrorC", {"center": v(9, 33) * mm, "radius": 0.5 * mm});
            skCircle(sketch, "E239.MirrorC", {"center": v(33, 33) * mm, "radius": 0.5 * mm});
            skCircle(sketch, "E240.MirrorC", {"center": v(27, 9) * mm, "radius": 0.5 * mm});
            skCircle(sketch, "E241.MirrorC", {"center": v(15, 57) * mm, "radius": 0.5 * mm});
            skCircle(sketch, "E242.MirrorC", {"center": v(15, 39) * mm, "radius": 0.5 * mm});
            skCircle(sketch, "E243.MirrorC", {"center": v(57, 15) * mm, "radius": 0.5 * mm});
            skCircle(sketch, "E244.MirrorC", {"center": v(3, -63) * mm, "radius": 0.5 * mm});
            skCircle(sketch, "E245.MirrorC", {"center": v(3, -39) * mm, "radius": 0.5 * mm});
            skCircle(sketch, "E246.MirrorC", {"center": v(33, -45) * mm, "radius": 0.5 * mm});
            skCircle(sketch, "E247.MirrorC", {"center": v(45, -3) * mm, "radius": 0.5 * mm});
            skCircle(sketch, "E248.MirrorC", {"center": v(27, -45) * mm, "radius": 0.5 * mm});
            skCircle(sketch, "E249.MirrorC", {"center": v(21, -51) * mm, "radius": 0.5 * mm});
            skCircle(sketch, "E250.MirrorC", {"center": v(27, -27) * mm, "radius": 0.5 * mm});
            skCircle(sketch, "E251.MirrorC", {"center": v(9, 57) * mm, "radius": 0.5 * mm});
            skCircle(sketch, "E252.MirrorC", {"center": v(45, 9) * mm, "radius": 0.5 * mm});
            skCircle(sketch, "E253.MirrorC", {"center": v(33, 57) * mm, "radius": 0.5 * mm});
            skCircle(sketch, "E254.MirrorC", {"center": v(27, 33) * mm, "radius": 0.5 * mm});
            skCircle(sketch, "E255.MirrorC", {"center": v(21, 9) * mm, "radius": 0.5 * mm});
            skCircle(sketch, "E256.MirrorC", {"center": v(9, 39) * mm, "radius": 0.5 * mm});
            skCircle(sketch, "E257.MirrorC", {"center": v(51, -27) * mm, "radius": 0.5 * mm});
            skCircle(sketch, "E258.MirrorC", {"center": v(51, 33) * mm, "radius": 0.5 * mm});
            skCircle(sketch, "E259.MirrorC", {"center": v(33, 39) * mm, "radius": 0.5 * mm});
            skCircle(sketch, "E260.MirrorC", {"center": v(27, 15) * mm, "radius": 0.5 * mm});
            skCircle(sketch, "E261.MirrorC", {"center": v(15, 63) * mm, "radius": 0.5 * mm});
            skCircle(sketch, "E262.MirrorC", {"center": v(3, -21) * mm, "radius": 0.5 * mm});
            skCircle(sketch, "E263.MirrorC", {"center": v(27, -33) * mm, "radius": 0.5 * mm});
            skCircle(sketch, "E264.MirrorC", {"center": v(27, -39) * mm, "radius": 0.5 * mm});
            skCircle(sketch, "E265.MirrorC", {"center": v(21, -27) * mm, "radius": 0.5 * mm});
            skCircle(sketch, "E266.MirrorC", {"center": v(51, 15) * mm, "radius": 0.5 * mm});
            skCircle(sketch, "E267.MirrorC", {"center": v(21, -9) * mm, "radius": 0.5 * mm});
            skCircle(sketch, "E268.MirrorC", {"center": v(21, -15) * mm, "radius": 0.5 * mm});
            skCircle(sketch, "E269.MirrorC", {"center": v(51, -3) * mm, "radius": 0.5 * mm});
            skCircle(sketch, "E270.MirrorC", {"center": v(63, -3) * mm, "radius": 0.5 * mm});
            skCircle(sketch, "E271.MirrorC", {"center": v(33, -3) * mm, "radius": 0.5 * mm});
            skCircle(sketch, "E272.MirrorC", {"center": v(9, 63) * mm, "radius": 0.5 * mm});
            skCircle(sketch, "E273.MirrorC", {"center": v(45, 15) * mm, "radius": 0.5 * mm});
            skCircle(sketch, "E274.MirrorC", {"center": v(27, 39) * mm, "radius": 0.5 * mm});
            skCircle(sketch, "E275.MirrorC", {"center": v(21, 15) * mm, "radius": 0.5 * mm});
            skCircle(sketch, "E276.MirrorC", {"center": v(27, 45) * mm, "radius": 0.5 * mm});
            skCircle(sketch, "E277.MirrorC", {"center": v(21, 21) * mm, "radius": 0.5 * mm});
            skCircle(sketch, "E278.MirrorC", {"center": v(39, 45) * mm, "radius": 0.5 * mm});
            skCircle(sketch, "E279.MirrorC", {"center": v(33, 21) * mm, "radius": 0.5 * mm});
            skCircle(sketch, "E280.MirrorC", {"center": v(15, 45) * mm, "radius": 0.5 * mm});
            skCircle(sketch, "E281.MirrorC", {"center": v(57, 21) * mm, "radius": 0.5 * mm});
            skCircle(sketch, "E282.MirrorC", {"center": v(9, -15) * mm, "radius": 0.5 * mm});
            skCircle(sketch, "E283.MirrorC", {"center": v(3, -57) * mm, "radius": 0.5 * mm});
            skCircle(sketch, "E284.MirrorC", {"center": v(9, 45) * mm, "radius": 0.5 * mm});
            skCircle(sketch, "E285.MirrorC", {"center": v(51, 39) * mm, "radius": 0.5 * mm});
            skCircle(sketch, "E286.MirrorC", {"center": v(33, 45) * mm, "radius": 0.5 * mm});
            skCircle(sketch, "E287.MirrorC", {"center": v(27, 21) * mm, "radius": 0.5 * mm});
            skCircle(sketch, "E288.MirrorC", {"center": v(63, -9) * mm, "radius": 0.5 * mm});
            skCircle(sketch, "E289.MirrorC", {"center": v(21, -57) * mm, "radius": 0.5 * mm});
            skCircle(sketch, "E290.MirrorC", {"center": v(3, -15) * mm, "radius": 0.5 * mm});
            skCircle(sketch, "E291.MirrorC", {"center": v(39, -15) * mm, "radius": 0.5 * mm});
            skCircle(sketch, "E292.MirrorC", {"center": v(57, -15) * mm, "radius": 0.5 * mm});
            skCircle(sketch, "E293.MirrorC", {"center": v(39, -9) * mm, "radius": 0.5 * mm});
            skCircle(sketch, "E294.MirrorC", {"center": v(51, 21) * mm, "radius": 0.5 * mm});
            skCircle(sketch, "E295.MirrorC", {"center": v(57, -21) * mm, "radius": 0.5 * mm});
            skCircle(sketch, "E296.MirrorC", {"center": v(3, -33) * mm, "radius": 0.5 * mm});
            skCircle(sketch, "E297.MirrorC", {"center": v(39, -21) * mm, "radius": 0.5 * mm});
            skCircle(sketch, "E298.MirrorC", {"center": v(9, -27) * mm, "radius": 0.5 * mm});
            skCircle(sketch, "E299.MirrorC", {"center": v(39, -33) * mm, "radius": 0.5 * mm});
            skCircle(sketch, "E300.MirrorC", {"center": v(21, -63) * mm, "radius": 0.5 * mm});
            skCircle(sketch, "E301.MirrorC", {"center": v(9, -33) * mm, "radius": 0.5 * mm});
            skCircle(sketch, "E302.MirrorC", {"center": v(57, -3) * mm, "radius": 0.5 * mm});
            skSolve(sketch);
        }
        {
            var Q0;
            Q0 = qSketchRegion(id + "F3", true);
            extrude(context, id + "F4", {"entities" : qUnion([Q0]), "operationType" : NewBodyOperationType.REMOVE, "endBound" : BoundingType.UP_TO_NEXT, "oppositeDirection" : true, "depth" : 25 * mm});
        }
        {
            var Q0;
            Q0=makeQuery(id+"F1.opExtrude","CAP_EDGE",EDGE,{"disambiguationData":[OSD([sQuery(id+"F0.wireOp",EDGE,"E0")])],"isStart":true});
            fillet(context, id + "F5", {"entities" : qUnion([Q0]), "radius" : 2 * mm, "tangentPropagation" : true, "allowEdgeOverflow" : false});
        }
        {
            var Q0;
            Q0=makeQuery(id+"F1.opExtrude","CAP_FACE",FACE,{"disambiguationData":[OSD([sQuery(id+"F0.wireOp",EDGE,"E0")])],"isStart":false});
            var sketch = newSketch(context, id + "F6", { "sketchPlane" : qUnion([Q0])});
            skCircle(sketch, "E303", {"center": v(0, 0) * mm, "radius": 69.85 * mm});
            skCircle(sketch, "E304", {"center": v(0, 0) * mm, "radius": 69.35 * mm});
            skSolve(sketch);
        }
        {
            var Q0;
            Q0 = qSketchRegion(id + "F6", true);
            extrude(context, id + "F7", {"entities" : qUnion([Q0]), "operationType" : NewBodyOperationType.REMOVE, "oppositeDirection" : true, "depth" : 2 * mm});
        }
    });
